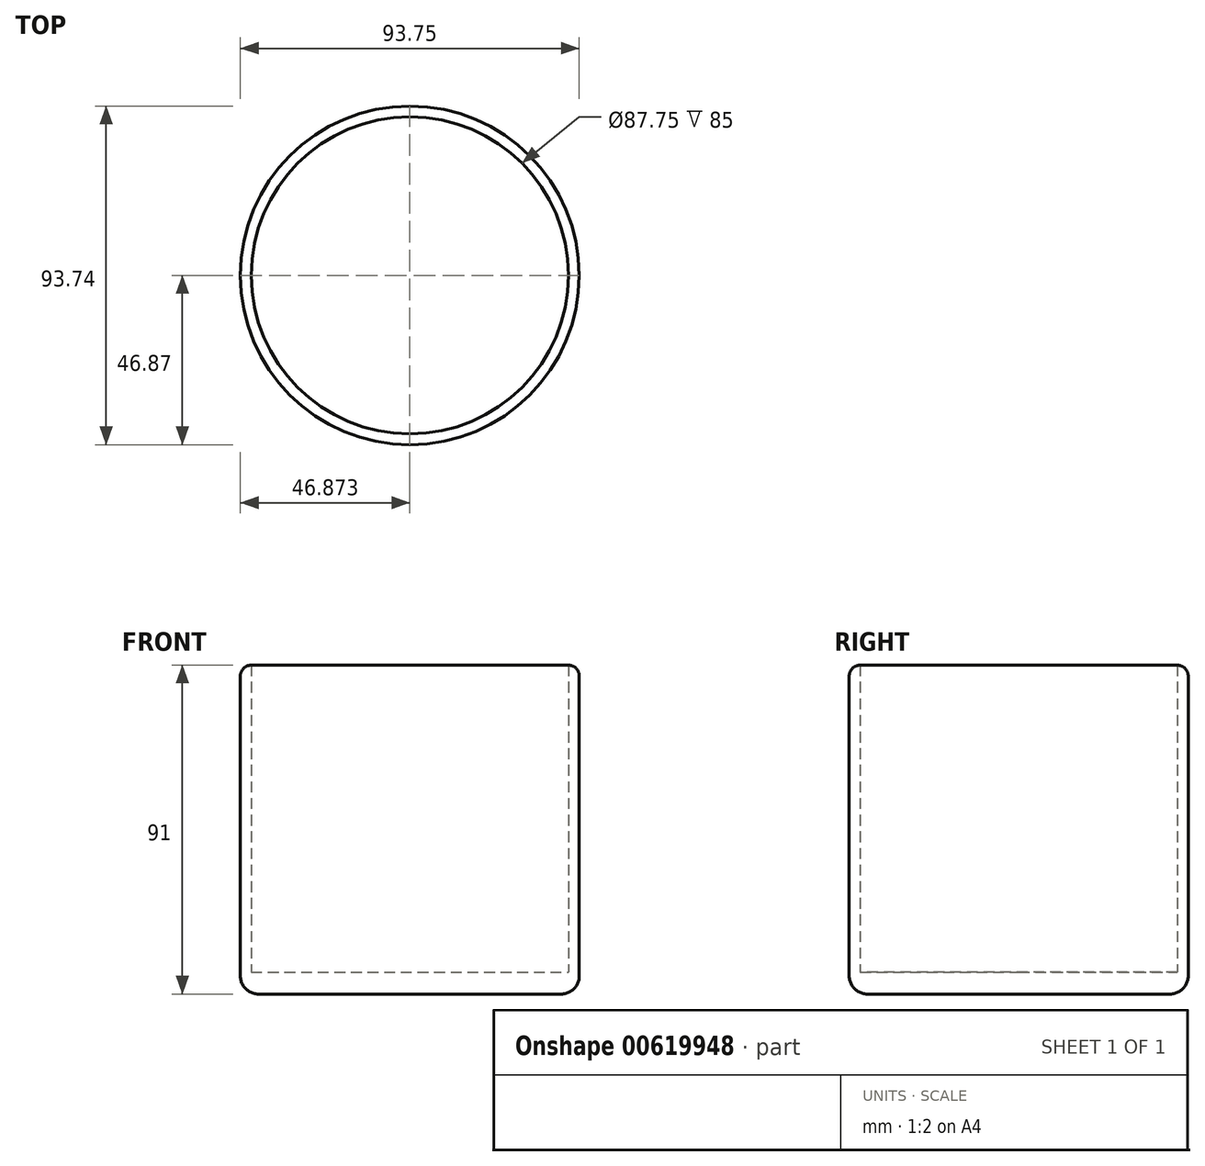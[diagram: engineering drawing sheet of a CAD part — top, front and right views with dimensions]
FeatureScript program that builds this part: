
annotation { "Feature Type Name" : "Feature", "Feature Type Description" : "" }
export const myFeature = defineFeature(function(context is Context, id is Id, definition is map)
    precondition{}
    {
        {
            var Q0;
            Q0=qCreatedBy(makeId("Front.planeOp"),FACE);
            var sketch = newSketch(context, id + "F0", { "sketchPlane" : qUnion([Q0])});
            skLineSegment(sketch, "E0", {"start": v(-94.5, 50) * mm, "end": v(-91.5, 50) * mm});
            skLineSegment(sketch, "E1", {"start": v(-94.5, 50) * mm, "end": v(-94.5, -41) * mm});
            skLineSegment(sketch, "E2", {"start": v(-91.5, 50) * mm, "end": v(-91.5, -35) * mm});
            skLineSegment(sketch, "E3", {"start": v(-91.5, -35) * mm, "end": v(-47.62, -35) * mm});
            skLineSegment(sketch, "E4", {"start": v(-94.5, -41) * mm, "end": v(-47.62, -41) * mm});
            skLineSegment(sketch, "E5", {"start": v(-47.62, -41) * mm, "end": v(-47.62, -35) * mm});
            skSolve(sketch);
        }
        {
            var Q0;
            Q0 = qSketchRegion(id + "F0", true);
            var Q1;
            Q1=sQuery(id+"F0.wireOp",EDGE,"E5");
            revolve(context, id + "F1", {"entities" : qUnion([Q0]), "axis" : qUnion([Q1]), "revolveType" : RevolveType.FULL});
        }
        {
            var Q0;
            Q0=makeQuery(id+"F1.opRevolve","SWEPT_EDGE",EDGE,{"disambiguationData":[OSD([sQuery(id+"F0.wireOp",EDGE,"E0"),sQuery(id+"F0.wireOp",EDGE,"E1")])]});
            fillet(context, id + "F2", {"entities" : qUnion([Q0]), "radius" : 3 * mm, "tangentPropagation" : true, "allowEdgeOverflow" : false});
        }
        {
            var Q0;
            Q0=makeQuery(id+"F1.opRevolve","SWEPT_EDGE",EDGE,{"disambiguationData":[OSD([sQuery(id+"F0.wireOp",EDGE,"E1"),sQuery(id+"F0.wireOp",EDGE,"E4")])]});
            fillet(context, id + "F3", {"entities" : qUnion([Q0]), "radius" : 5 * mm, "tangentPropagation" : true, "allowEdgeOverflow" : false});
        }
    });
